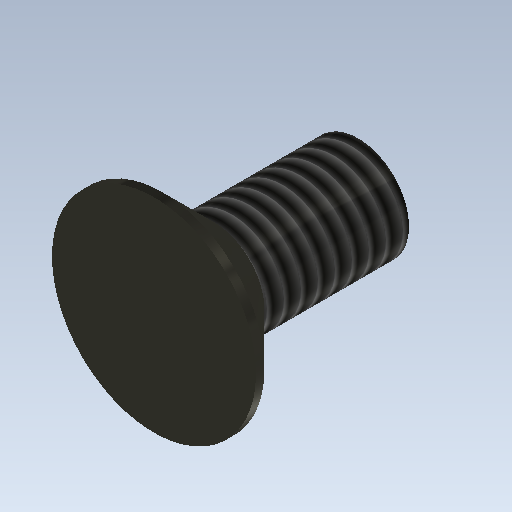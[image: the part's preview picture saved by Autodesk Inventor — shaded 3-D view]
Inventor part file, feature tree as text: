
AUTODESK INVENTOR PART (.ipt)
format: ipt  version: 2020.2 (Build 242310000, 310)  size: 143,360 bytes
history: native  units: mm
features: extrude x3, sketch x3, other x1, thread x1, chamfer x1
ambient origin geometry x1: Origin
bodies: Body1 (feature_tree)
feature tree (9):
  other  "ソリッド1"
  extrude  "押し出し1"  Depth=3.0mm
  extrude  "押し出し2"  Depth=6.0mm TaperAngle=0.0deg
  thread  "ねじ1"
  chamfer  "面取り1"  Distance=6.0mm
  extrude  "押し出し4"  Depth=1.75mm TaperAngle=0.0deg
  sketch  "スケッチ1"
  sketch  "スケッチ2"
  sketch  "スケッチ4"
